# Revit family: Site-Fencing-Tymetal_Corp-Box_Frame_Cantilever_Slide_Gate-Chain_Link
name_source: partatom
category: Site
revit_build: Autodesk Revit 2015 (Build: 20140606_1530(x64)
units: mm (PartAtom-declared; Revit-internal decimal feet)

## types (1)
- Standard
    Additional Posts = 3
    Assembly Code = G2040100
    Barb Arms and Wires = Yes
    Barb Height = 1' - 3"
    Between Posts = 2' - 11"
    Bottom Guide Cover = No
    Catch Assembly Height Above Grade = 3' - 6"
    Chain Link Panel Count = 4
    Chain Link Panel Length = 5' - 7"
    Clear Opening = 15' - 0"
    Counter Balance Length = 7' - 6"
    Description = Fortress Box Frame Cantilever Slide Gate with Chain Link Fencing
    Fence Offset from Grade = 0' - 5"
    Finish = Metal - Tymetal - Aluminum
    Finish Note = For additional powder coat color options, please contact Tymetal
    Front Additional Posts = 2
    Front Chain Link Panel Count = 3
    Front Panel Length = 4' - 10 29/32"
    Gate Documentation Link = http://www.tymetal.com
    Gate Height Clearances = 8' - 0"
    Hardware Finish = Metal - Tymetal - Aluminum
    Height = 8' - 0"
    Length = 22' - 6"
    Manufacturer = Tymetal Corp.
    Model = Chain Link
    Mount Clamp Extension from Gate = 0' - 2"
    Notes = Single Clear Opening up to 60' and Double Clear Openings up to 120'
    Options = Barb Arms are Optional; Barb Wires by Others
    Panel Height = 9' - 3"
    Post Diameter = 0' - 4"
    Post Height = 9' - 9"
    Post Radius = 0' - 2"
    Post Spacing = 6' - 7"
    Product Documentation Link = http://www.tymetal.com
    Product Page URL = http://www.tymetal.com
    Product data url = https://bimobject.com
    Single Gate Clearances = 15' - 0"
    URL = http://www.tymetal.com

## geometry (parser evidence)
native form markers: Sweep x48
no freeform markers — native parametric forms only
